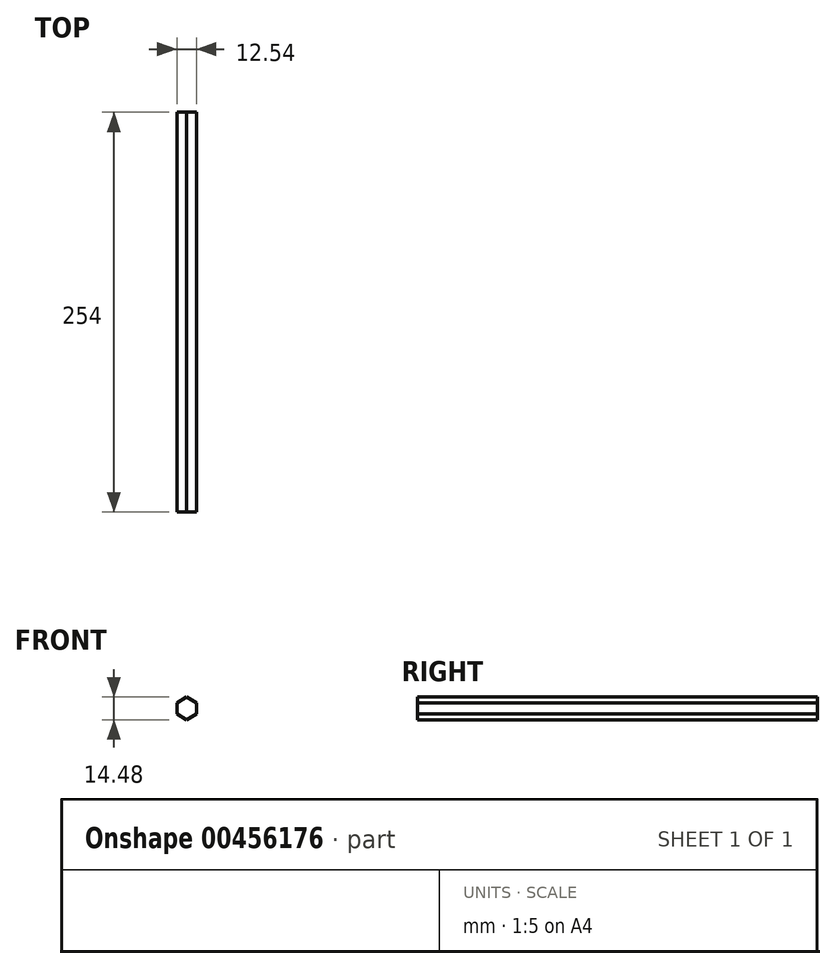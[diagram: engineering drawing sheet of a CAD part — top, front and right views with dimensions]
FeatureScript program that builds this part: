
annotation { "Feature Type Name" : "Feature", "Feature Type Description" : "" }
export const myFeature = defineFeature(function(context is Context, id is Id, definition is map)
    precondition{}
    {
        {
            var Q0;
            Q0=qCreatedBy(makeId("Front.planeOp"),FACE);
            var sketch = newSketch(context, id + "F0", { "sketchPlane" : qUnion([Q0])});
            skCircle(sketch, "E0.cCircle", {"center": v(0, 0) * mm, "radius": 7.24 * mm, "construction": true});
            skLineSegment(sketch, "E0.0", {"start": v(0, 7.24) * mm, "end": v(6.27, 3.62) * mm});
            skLineSegment(sketch, "E0.1", {"start": v(6.27, 3.62) * mm, "end": v(6.27, -3.62) * mm});
            skLineSegment(sketch, "E0.2", {"start": v(6.27, -3.62) * mm, "end": v(0, -7.24) * mm});
            skLineSegment(sketch, "E0.3", {"start": v(0, -7.24) * mm, "end": v(-6.27, -3.62) * mm});
            skLineSegment(sketch, "E0.4", {"start": v(-6.27, -3.62) * mm, "end": v(-6.27, 3.62) * mm});
            skLineSegment(sketch, "E0.5", {"start": v(-6.27, 3.62) * mm, "end": v(0, 7.24) * mm});
            skSolve(sketch);
        }
        {
            var Q0;
            Q0=makeQuery(id+"F0.imprint","IMPRINT",FACE,{"disambiguationData":[TD([[makeQuery(id+"F0.imprint","IMPRINT",EDGE,{"derivedFrom":sQuery(id+"F0.wireOp",EDGE,"E0.0")}),-1.0]])]});
            extrude(context, id + "F1", {"entities" : qUnion([Q0]), "depth" : 254 * mm});
        }
    });
